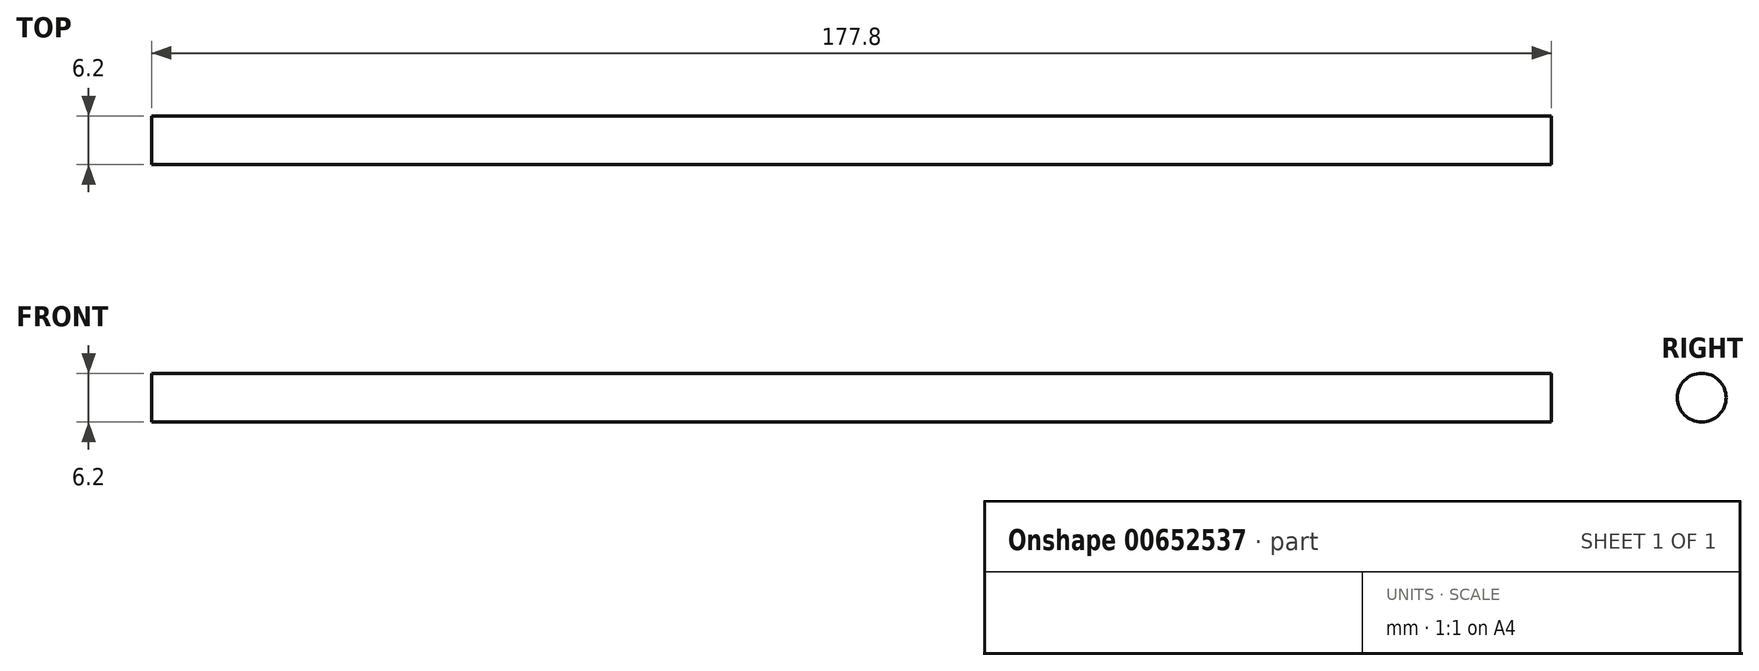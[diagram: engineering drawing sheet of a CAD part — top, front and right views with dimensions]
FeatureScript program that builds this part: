
annotation { "Feature Type Name" : "Feature", "Feature Type Description" : "" }
export const myFeature = defineFeature(function(context is Context, id is Id, definition is map)
    precondition{}
    {
        {
            var Q0;
            Q0=qCreatedBy(makeId("Right.planeOp"),FACE);
            var sketch = newSketch(context, id + "F0", { "sketchPlane" : qUnion([Q0])});
            skCircle(sketch, "E0", {"center": v(0, 0) * mm, "radius": 3.1 * mm});
            skSolve(sketch);
        }
        {
            var Q0;
            Q0=makeQuery(id+"F0.imprint","IMPRINT",FACE,{"disambiguationData":[TD([[makeQuery(id+"F0.imprint","IMPRINT",EDGE,{"derivedFrom":sQuery(id+"F0.wireOp",EDGE,"E0")}),1.0]])]});
            extrude(context, id + "F1", {"entities" : qUnion([Q0]), "depth" : 88.9 * mm, "offsetDistance" : 25.4 * mm, "hasSecondDirection" : true, "secondDirectionOppositeDirection" : true, "secondDirectionDepth" : 88.9 * mm});
        }
    });
